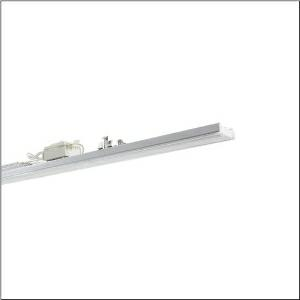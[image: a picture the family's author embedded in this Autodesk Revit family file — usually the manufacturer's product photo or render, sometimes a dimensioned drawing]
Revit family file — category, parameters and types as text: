
# Revit family: licross_r__11_recessed_mo_51tl18cn49xg_d751
name_source: partatom
category: Lighting Fixtures
units: mm (PartAtom-declared; Revit-internal decimal feet)

## family parameters
Cut with Voids When Loaded = No
Host = Face
Light Source = No
Part Type = Normal
Room Calculation Point = No
Round Connector Dimension = Use Diameter
Shared = No

## types (1)
- --- (1 x LED, 9040 lm, 49.3 W, 4000K)
    Apparent Load = 49 VA
    CIE Flux Codes = 83 96 99 100 100
    Color Rendering = 80
    Color Temperature = 4000K
    Default Elevation = 1800 mm
    Description = Licross® 11 Recessed MO, luminaire insert, of sheet steel, coil coated, white, length: 1.500mm, width: 66mm, height: 67mm, LED rated luminous flux: 9.040lm, light colour: 840, control gear: ON/OFF Multilumen, CLOi, with plug, 3-pole, with phase selection, mains connection: 220..240V, AC, 50/60Hz, start of lifetime: 49W, end of service life: 55W, internal wiring halogen-free, primary light control with lens, of plastic, primary optical cover: cover, of PMMA, light emission: direct distribution, primary light characteristic: symmetric, protection rating (complete): IP40, insulation class (complete): insulation class I (protective earthing), certification: CE, ENEC, VDE, UKCA, protection symbol: D if used in an environment without relevant dust loads with corresponding accessories, impact resistance: IK06, permissible ambient temperature for indoor applications: -35..+40°C, corresponds to IFS (International Featured Standards) requirements for safety and quality in the food industry, reducing of maximum allowable ambient temperature of 5°C with ceiling mounting, LABS conformity tested according to VDMA 24364:2018-05, packaging unit: 1 piece
    Height = 58 mm
    Lamp = 1 x LED
    Lamp Light Flux = 9040 lm
    Lamp Power = 49.3 W
    Lamp count = 1
    Length = 1500 mm
    Luminous efficacy = 183 lm/W
    Manufacturer = Siteco
    ModVariant = No
    Model = 51TL18CN49XG
    Mounting Place = Ceiling
    Mounting Type = Pendant
    Number of Poles = 1
    OnlyDefault = Yes
    Power Factor = 1
    Product Name = Licross® 11 Recessed MO
    Product group = luminaire insert | ceiling pendant
    ProductGroupID = 902
    Protection Class = Protection class I
    Protection Degree = IP 40
    RLX_Detail_Level = 1
    RLX_Emergency_Light_Flux = 0 lm
    RLX_Emergency_Type = 0
    RLX_Emergency_Type_DB = No
    RlxData = <blob elided: 22297 chars, md5=466e4f65>
    Socket = socket
    Standby Power = 0 W
    System Light Flux = 9040 lm
    System Power = 49 W
    Type Comments = factory setting: luminous flux: 100 % | (A | C | E) | 113 mA
    Type Image = l_1296930.jpg
    URL = http://relux.com
    VarID = @adj_106131
    Voltage = 0 V
    Weight = 0.00 kg
    Width = 66 mm

## geometry (parser evidence)
native form markers: Blend x4, Sweep x12
no freeform markers — native parametric forms only
